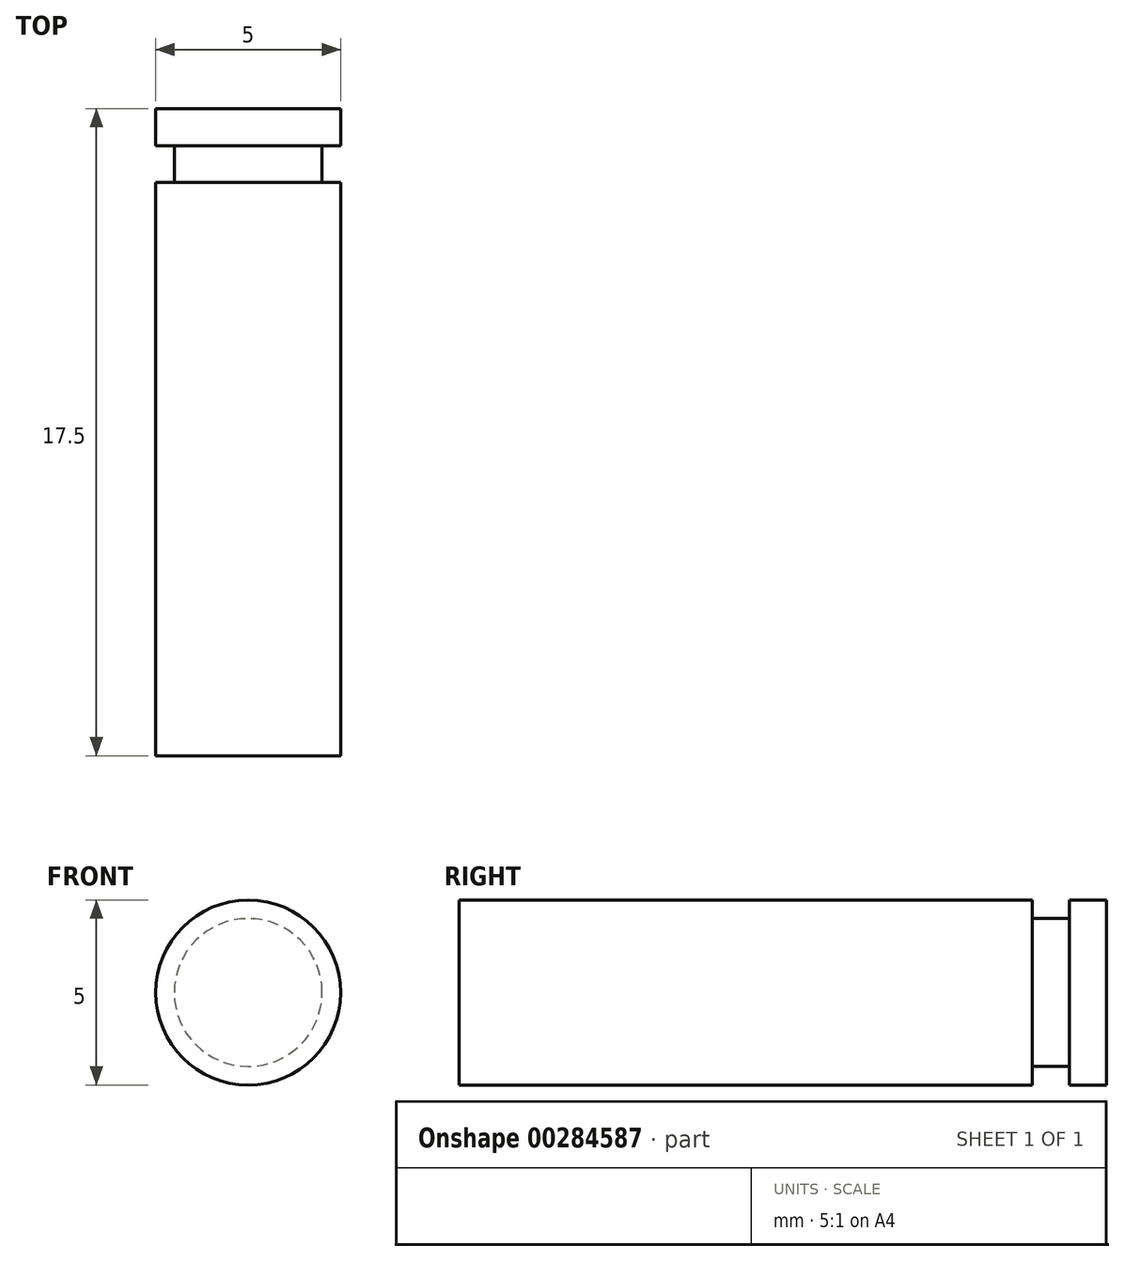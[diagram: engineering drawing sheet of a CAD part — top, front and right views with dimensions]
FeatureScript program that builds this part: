
annotation { "Feature Type Name" : "Feature", "Feature Type Description" : "" }
export const myFeature = defineFeature(function(context is Context, id is Id, definition is map)
    precondition{}
    {
        {
            var Q0;
            Q0=qCreatedBy(makeId("Right.planeOp"),FACE);
            var sketch = newSketch(context, id + "F0", { "sketchPlane" : qUnion([Q0])});
            skLineSegment(sketch, "E0", {"start": v(0, 0) * mm, "end": v(17.5, 0) * mm});
            skLineSegment(sketch, "E1", {"start": v(17.5, 0) * mm, "end": v(17.5, 2.5) * mm});
            skLineSegment(sketch, "E2", {"start": v(17.5, 2.5) * mm, "end": v(16.5, 2.5) * mm});
            skLineSegment(sketch, "E3", {"start": v(0, 2.5) * mm, "end": v(0, 0) * mm});
            skLineSegment(sketch, "E4", {"start": v(15.5, 2.5) * mm, "end": v(15.5, 2) * mm});
            skLineSegment(sketch, "E5", {"start": v(15.5, 2) * mm, "end": v(16.5, 2) * mm});
            skLineSegment(sketch, "E6", {"start": v(16.5, 2) * mm, "end": v(16.5, 2.5) * mm});
            skLineSegment(sketch, "E7.trimOffspring", {"start": v(15.5, 2.5) * mm, "end": v(0, 2.5) * mm});
            skLineSegment(sketch, "E8", {"start": v(0, 0) * mm, "end": v(36.3, 0) * mm, "construction": true});
            skSolve(sketch);
        }
        {
            var Q0;
            Q0=qSketchRegion(id+"F0",true);
            var Q1;
            Q1=sQuery(id+"F0.wireOp",EDGE,"E8");
            revolve(context, id + "F1", {"entities" : qUnion([Q0]), "axis" : qUnion([Q1]), "revolveType" : RevolveType.FULL});
        }
    });
